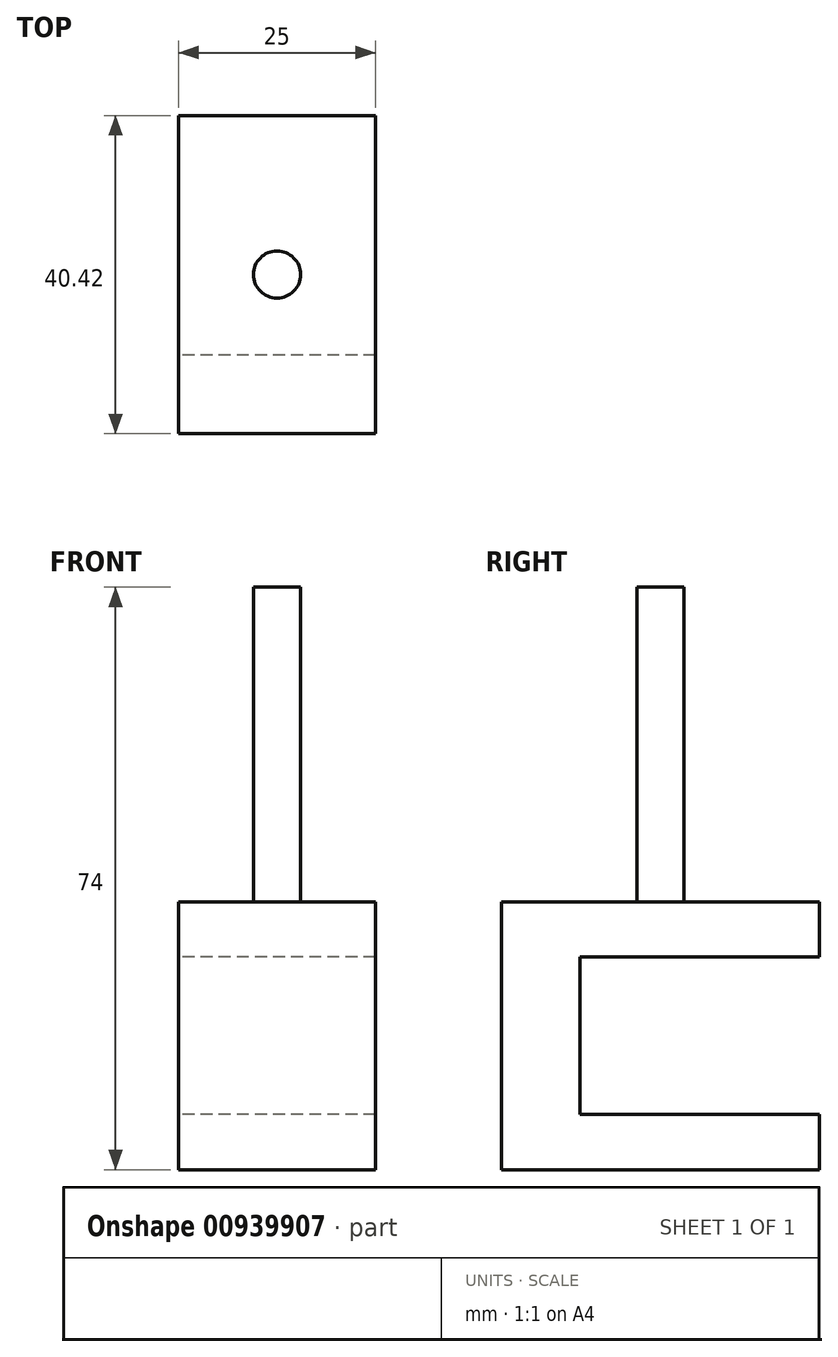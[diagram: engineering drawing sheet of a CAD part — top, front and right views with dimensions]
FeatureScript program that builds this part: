
annotation { "Feature Type Name" : "Feature", "Feature Type Description" : "" }
export const myFeature = defineFeature(function(context is Context, id is Id, definition is map)
    precondition{}
    {
        {
            var Q0;
            Q0=qCreatedBy(makeId("Right.planeOp"),FACE);
            var sketch = newSketch(context, id + "F0", { "sketchPlane" : qUnion([Q0])});
            skLineSegment(sketch, "E0", {"start": v(0, 10) * mm, "end": v(0, -10) * mm});
            skLineSegment(sketch, "E1", {"start": v(0, 10) * mm, "end": v(30.42, 10) * mm});
            skLineSegment(sketch, "E2", {"start": v(30.42, 10) * mm, "end": v(30.42, 17) * mm});
            skLineSegment(sketch, "E3", {"start": v(30.42, 17) * mm, "end": v(-10, 17) * mm});
            skLineSegment(sketch, "E4", {"start": v(-10, 17) * mm, "end": v(-10, -17) * mm});
            skLineSegment(sketch, "E5", {"start": v(-10, -17) * mm, "end": v(30.42, -17) * mm});
            skLineSegment(sketch, "E6", {"start": v(30.42, -17) * mm, "end": v(30.42, -10) * mm});
            skLineSegment(sketch, "E7", {"start": v(30.42, -10) * mm, "end": v(0, -10) * mm});
            skSolve(sketch);
        }
        {
            var Q0;
            Q0=makeQuery(id+"F0.imprint","IMPRINT",FACE,{"disambiguationData":[TD([[makeQuery(id+"F0.imprint","IMPRINT",EDGE,{"derivedFrom":sQuery(id+"F0.wireOp",EDGE,"E0")}),-1.0]])]});
            extrude(context, id + "F1", {"entities" : qUnion([Q0]), "depth" : 25 * mm, "offsetDistance" : 25 * mm});
        }
        {
            var Q0;
            Q0=makeQuery(id+"F1.opExtrude","SWEPT_FACE",FACE,{"disambiguationData":[OSD([sQuery(id+"F0.wireOp",EDGE,"E3")])]});
            var sketch = newSketch(context, id + "F2", { "sketchPlane" : qUnion([Q0])});
            skCircle(sketch, "E8", {"center": v(12.5, 10.2) * mm, "radius": 3 * mm});
            skPoint(sketch, "E8.centerSnap0", {"position": v(25, 10.2) * mm});
            skPoint(sketch, "E8.centerSnap1", {"position": v(12.5, -10) * mm});
            skSolve(sketch);
        }
        {
            var Q0;
            Q0=makeQuery(id+"F2.imprint","IMPRINT",FACE,{"disambiguationData":[TD([[makeQuery(id+"F2.imprint","IMPRINT",EDGE,{"derivedFrom":sQuery(id+"F2.wireOp",EDGE,"E8")}),1.0]])]});
            extrude(context, id + "F3", {"entities" : qUnion([Q0]), "operationType" : NewBodyOperationType.ADD, "depth" : 40 * mm, "offsetDistance" : 25 * mm});
        }
    });
